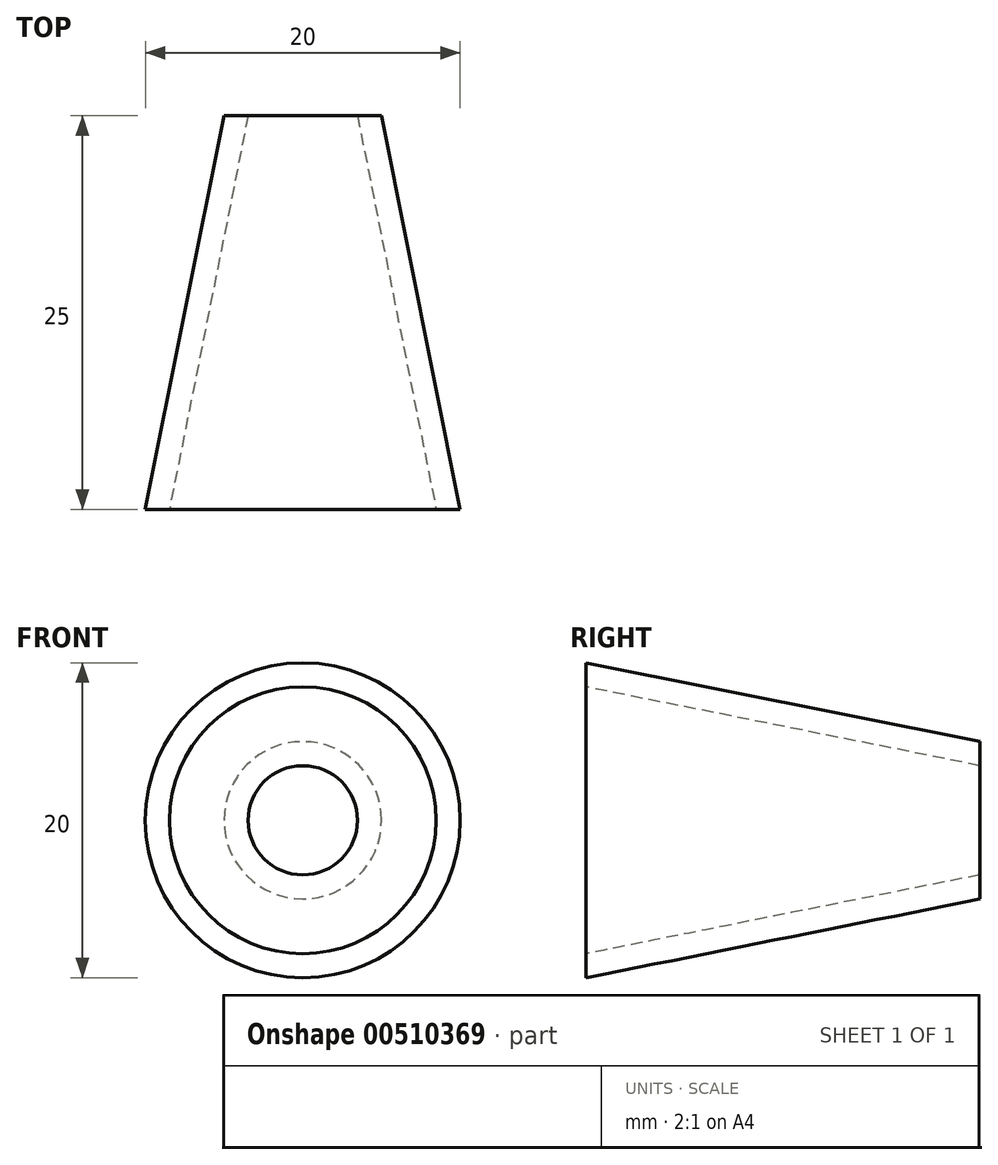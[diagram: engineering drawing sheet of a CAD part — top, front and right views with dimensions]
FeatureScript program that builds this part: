
annotation { "Feature Type Name" : "Feature", "Feature Type Description" : "" }
export const myFeature = defineFeature(function(context is Context, id is Id, definition is map)
    precondition{}
    {
        {
            var Q0;
            Q0=qCreatedBy(makeId("Front.planeOp"),FACE);
            var sketch = newSketch(context, id + "F0", { "sketchPlane" : qUnion([Q0])});
            skCircle(sketch, "E0", {"center": v(-40.16, 37.45) * mm, "radius": 10 * mm});
            skSolve(sketch);
        }
        {
            var Q0;
            Q0=makeQuery(id+"F0.imprint","IMPRINT",FACE,{"disambiguationData":[TD([[makeQuery(id+"F0.imprint","IMPRINT",EDGE,{"derivedFrom":sQuery(id+"F0.wireOp",EDGE,"E0")}),1.0]])]});
            extrude(context, id + "F1", {"entities" : qUnion([Q0]), "depth" : 25 * mm});
        }
        {
            var Q0;
            Q0=makeQuery(id+"F1.opExtrude","CAP_FACE",FACE,{"disambiguationData":[OSD([sQuery(id+"F0.wireOp",EDGE,"E0")])],"isStart":true});
            var sketch = newSketch(context, id + "F2", { "sketchPlane" : qUnion([Q0])});
            skCircle(sketch, "E1", {"center": v(40.16, 37.45) * mm, "radius": 5 * mm});
            skSolve(sketch);
        }
        {
            var Q1;
            Q1=makeQuery(id+"F2.imprint","IMPRINT",FACE,{"disambiguationData":[TD([[makeQuery(id+"F2.imprint","IMPRINT",EDGE,{"derivedFrom":sQuery(id+"F2.wireOp",EDGE,"E1")}),1.0]])]});
            var Q2;
            Q2=makeQuery(id+"F1.opExtrude","CAP_FACE",FACE,{"disambiguationData":[OSD([sQuery(id+"F0.wireOp",EDGE,"E0")])],"isStart":false});
            loft(context, id + "F3", {"operationType" : NewBodyOperationType.INTERSECT, "sheetProfilesArray" : [{ "sheetProfileEntities" : qUnion([Q1]) }, { "sheetProfileEntities" : qUnion([Q2]) }]});
        }
        {
            var Q0;
            Q0=makeQuery(id+"F1.opExtrude","CAP_FACE",FACE,{"disambiguationData":[OSD([sQuery(id+"F0.wireOp",EDGE,"E0")])],"isStart":false});
            var Q1;
            Q1=makeQuery(id+"F1.opExtrude","CAP_FACE",FACE,{"disambiguationData":[OSD([sQuery(id+"F0.wireOp",EDGE,"E0")])],"isStart":true});
            shell(context, id + "F4", {"entities" : qUnion([Q0, Q1]), "thickness" : 1.5 * mm});
        }
    });
